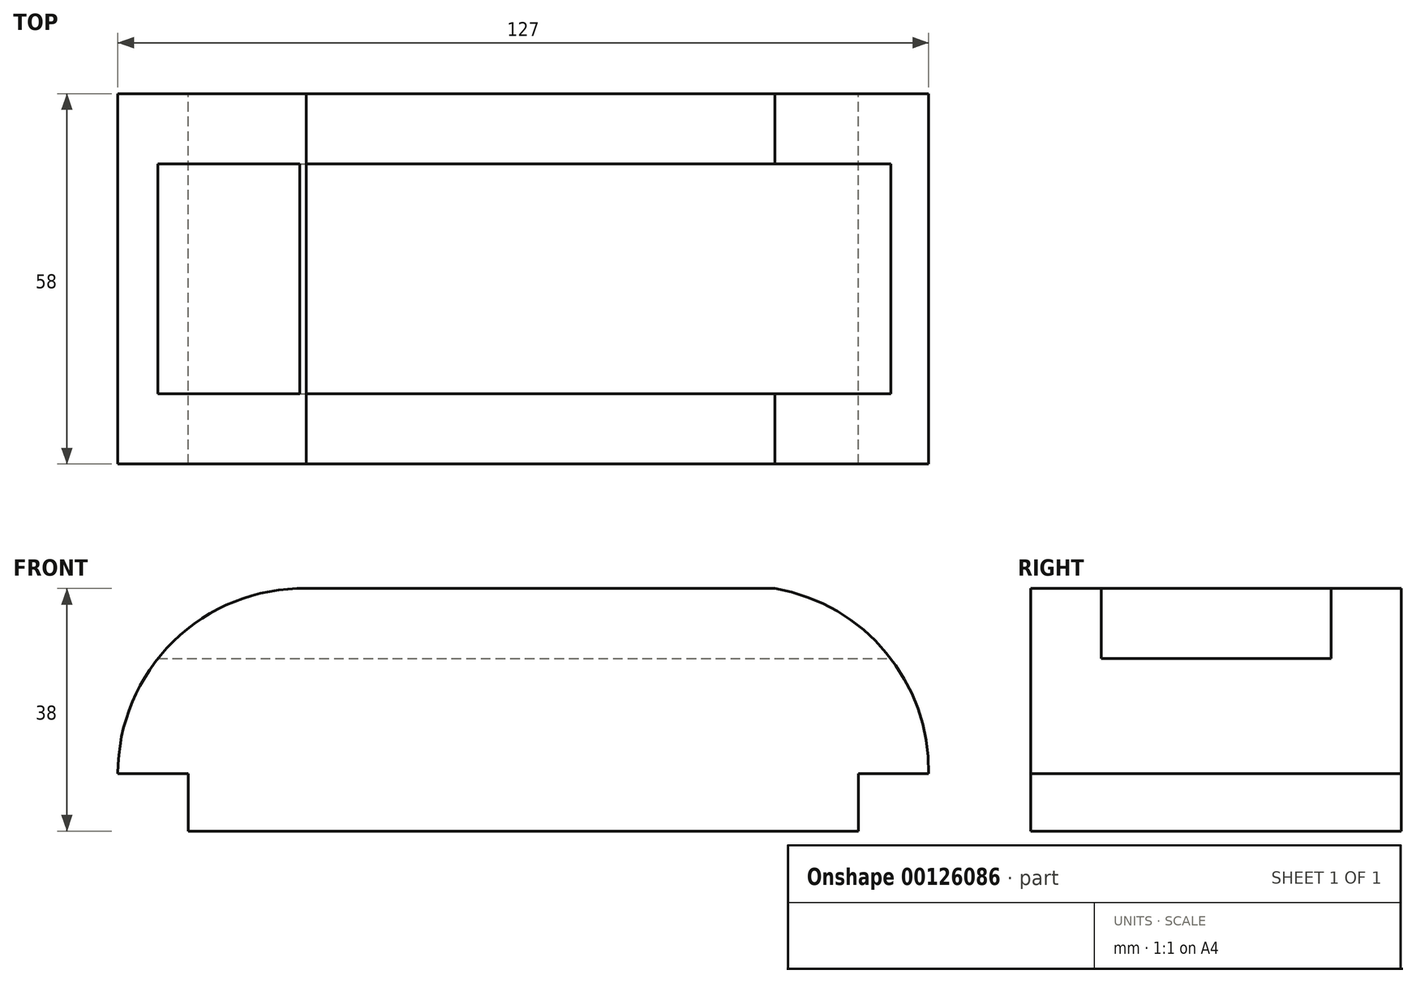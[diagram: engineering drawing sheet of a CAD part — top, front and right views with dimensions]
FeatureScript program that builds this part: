
annotation { "Feature Type Name" : "Feature", "Feature Type Description" : "" }
export const myFeature = defineFeature(function(context is Context, id is Id, definition is map)
    precondition{}
    {
        {
            var Q0;
            Q0=qCreatedBy(makeId("Front.planeOp"),FACE);
            var sketch = newSketch(context, id + "F0", { "sketchPlane" : qUnion([Q0])});
            skLineSegment(sketch, "E0", {"start": v(-55.5, 0) * mm, "end": v(49.5, 0) * mm});
            skLineSegment(sketch, "E1", {"start": v(49.5, 0) * mm, "end": v(49.5, 9) * mm});
            skLineSegment(sketch, "E2", {"start": v(-55.5, 0) * mm, "end": v(-55.5, 9) * mm});
            skLineSegment(sketch, "E3", {"start": v(-55.5, 9) * mm, "end": v(-66.5, 9) * mm});
            skLineSegment(sketch, "E4", {"start": v(49.5, 9) * mm, "end": v(60.5, 9) * mm});
            skLineSegment(sketch, "E5", {"start": v(-36.99, 38) * mm, "end": v(36.43, 38) * mm});
            skArc(sketch, "E6", {"start": v(-36.99, 38) * mm, "mid": v(-57.83, 29.7) * mm, "end": v(-66.5, 9) * mm});
            skArc(sketch, "E7", {"start": v(60.5, 9) * mm, "mid": v(53.81, 27.94) * mm, "end": v(36.43, 38) * mm});
            skLineSegment(sketch, "E8", {"start": v(0, 52.64) * mm, "end": v(0, -24.05) * mm, "construction": true});
            skSolve(sketch);
        }
        {
            var Q0;
            Q0=makeQuery(id+"F0.imprint","IMPRINT",FACE,{"disambiguationData":[TD([[makeQuery(id+"F0.imprint","IMPRINT",EDGE,{"derivedFrom":sQuery(id+"F0.wireOp",EDGE,"E0")}),1.0]])]});
            extrude(context, id + "F1", {"entities" : qUnion([Q0]), "endBound" : BoundingType.SYMMETRIC, "depth" : 58 * mm});
        }
        {
            var Q0;
            Q0=qCreatedBy(makeId("Right.planeOp"),FACE);
            var sketch = newSketch(context, id + "F2", { "sketchPlane" : qUnion([Q0])});
            skLineSegment(sketch, "E9.bottom", {"start": v(-18, 38) * mm, "end": v(18, 38) * mm});
            skLineSegment(sketch, "E9.top", {"start": v(-18, 27) * mm, "end": v(18, 27) * mm});
            skLineSegment(sketch, "E9.left", {"start": v(-18, 38) * mm, "end": v(-18, 27) * mm});
            skLineSegment(sketch, "E9.right", {"start": v(18, 38) * mm, "end": v(18, 27) * mm});
            skLineSegment(sketch, "E10", {"start": v(0, 43.27) * mm, "end": v(0, 20.52) * mm, "construction": true});
            skSolve(sketch);
        }
        {
            var Q0;
            Q0 = qSketchRegion(id + "F2", true);
            extrude(context, id + "F3", {"entities" : qUnion([Q0]), "operationType" : NewBodyOperationType.REMOVE, "endBound" : BoundingType.THROUGH_ALL, "oppositeDirection" : true, "depth" : 25 * mm, "hasSecondDirection" : true, "secondDirectionBound" : SecondDirectionBoundingType.THROUGH_ALL, "secondDirectionOppositeDirection" : false, "secondDirectionDepth" : 25 * mm});
        }
    });
